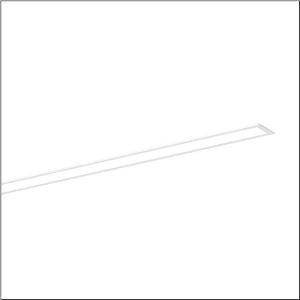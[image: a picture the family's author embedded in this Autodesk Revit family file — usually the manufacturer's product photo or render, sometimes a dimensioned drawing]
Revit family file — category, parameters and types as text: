
# Revit family: silica_r__21_51mx10dc45wb_eef5
name_source: partatom
category: Lighting Fixtures
units: mm (PartAtom-declared; Revit-internal decimal feet)

## family parameters
Cut with Voids When Loaded = No
Host = Face
Light Source = No
Part Type = Normal
Room Calculation Point = No
Round Connector Dimension = Use Diameter
Shared = No

## types (1)
- --- (1 x LED, 6000 lm, 40.1 W, 4000K)
    Apparent Load = 40 VA
    CIE Flux Codes = 48 79 96 100 100
    Color Rendering = 80
    Color Temperature = 4000K
    Default Elevation = 1800 mm
    Description = Silica® 21, office luminaire, primary optical cover: cover, of PMMA, opal, light emission: direct distribution, primary light characteristic: symmetric, installation type: recessed, LED, rated luminous flux: 6.000lm, luminous efficacy: 150lm/W, light colour: 840, colour temperature: 4000K, with terminal, 3+2-pole, max. 2.5mm², mains connection: 220..240V, AC, 50/60Hz, rated input power: 40.1W, luminaire housing, of aluminium, traffic white (RAL 9016), length: 3.028mm, width: 79mm, height: 53mm, protection rating (complete): IP20, insulation class (complete): insulation class I (protective earthing), certification: CE, permissible operating ambient temperature: 0..+35°C, standard: EN 50419, packaging unit: 1 piece
    Height = 0 mm  [stored 0 ft]
    Lamp = 1 x LED
    Lamp Light Flux = 6000 lm
    Lamp Power = 40.1 W
    Lamp count = 1
    Length = 3027 mm
    Luminous efficacy = 150 lm/W
    Manufacturer = Siteco
    ModVariant = No
    Model = 51MX10DC45WB
    Mounting Place = Ceiling
    Mounting Type = Recessed
    Number of Poles = 1
    OnlyDefault = Yes
    Power Factor = 1
    Product Name = Silica® 21
    Product group = office luminaire | ceiling recessed
    ProductGroupID = 401
    Protection Class = Protection class I
    Protection Degree = IP 20
    RLX_Detail_Level = 1
    RLX_Emergency_Light_Flux = 0 lm
    RLX_Emergency_Type = 0
    RLX_Emergency_Type_DB = No
    RlxData = <blob elided: 21117 chars, md5=6a4ae97d>
    Socket = socket
    Standby Power = 0 W
    System Light Flux = 6000 lm
    System Power = 40 W
    Type Comments = factory setting: luminous flux: 100 % | dim-lin: 254 | 218 mA
    Type Image = l_1313615.jpg
    URL = http://relux.com
    VarID = @adj_065751
    Voltage = 0 V
    Weight = 0.00 kg
    Width = 79 mm

note: [stored X ft] marks values corroborated as IEEE doubles in the binary element streams (Revit-internal decimal feet)

## geometry (parser evidence)
native form markers: Blend x4, Sweep x11
no freeform markers — native parametric forms only
